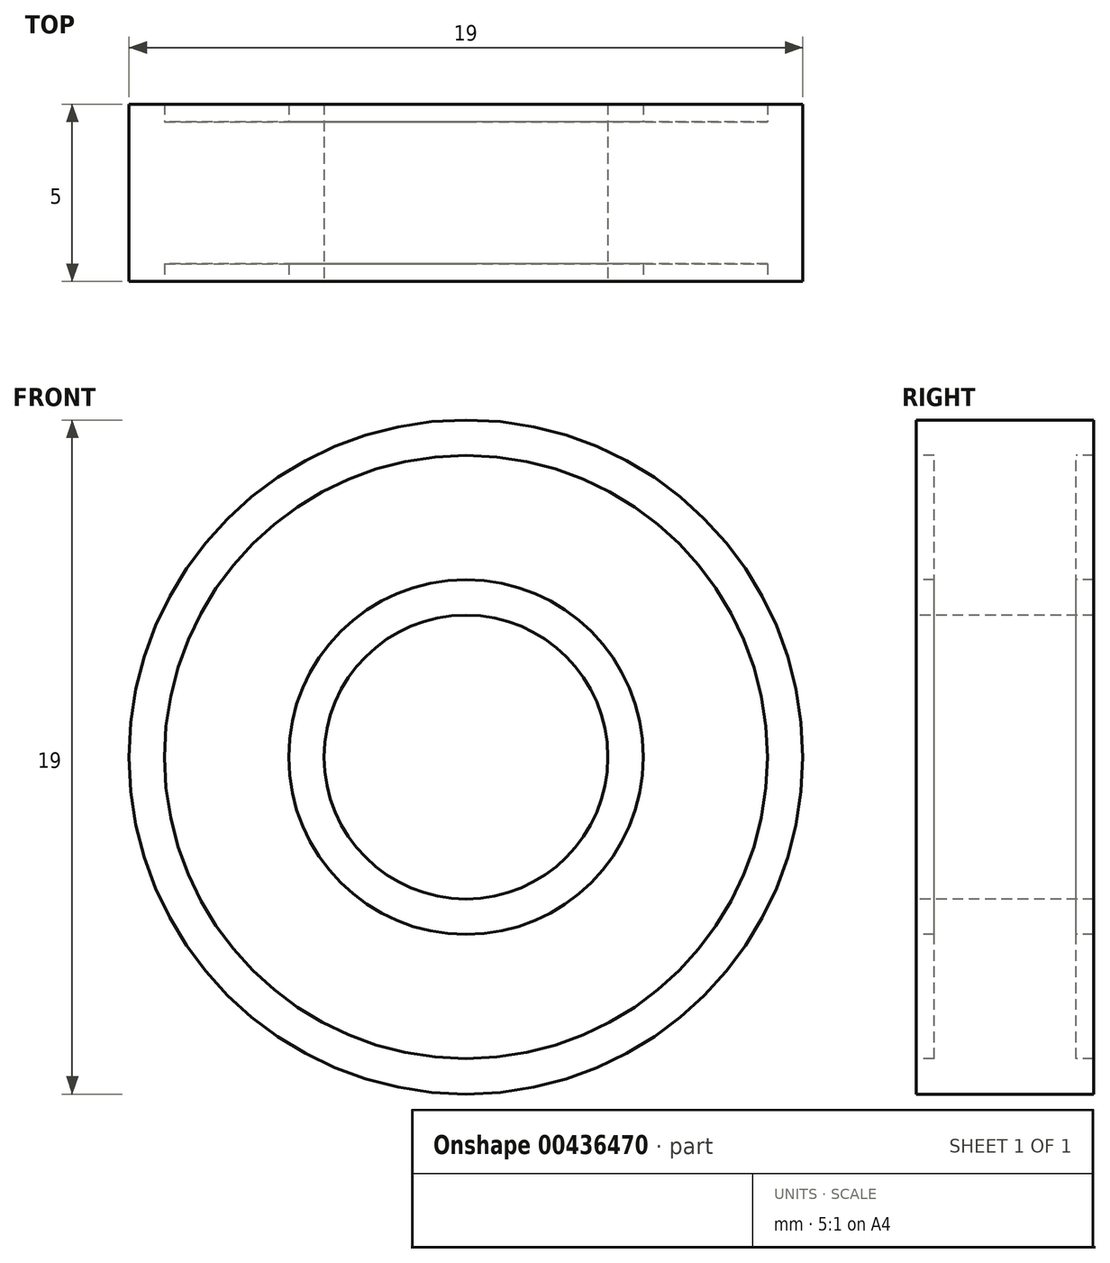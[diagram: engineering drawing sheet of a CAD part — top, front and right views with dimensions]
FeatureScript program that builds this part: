
annotation { "Feature Type Name" : "Feature", "Feature Type Description" : "" }
export const myFeature = defineFeature(function(context is Context, id is Id, definition is map)
    precondition{}
    {
        {
            var Q0;
            Q0=qCreatedBy(makeId("Right.planeOp"),FACE);
            var sketch = newSketch(context, id + "F0", { "sketchPlane" : qUnion([Q0])});
            skLineSegment(sketch, "E0", {"start": v(-2.5, 4) * mm, "end": v(2.5, 4) * mm});
            skLineSegment(sketch, "E1", {"start": v(2.5, 4) * mm, "end": v(2.5, 5) * mm});
            skLineSegment(sketch, "E2", {"start": v(2.5, 5) * mm, "end": v(2, 5) * mm});
            skLineSegment(sketch, "E3", {"start": v(2, 5) * mm, "end": v(2, 8.5) * mm});
            skLineSegment(sketch, "E4", {"start": v(2, 8.5) * mm, "end": v(2.5, 8.5) * mm});
            skLineSegment(sketch, "E5", {"start": v(2.5, 8.5) * mm, "end": v(2.5, 9.5) * mm});
            skLineSegment(sketch, "E6", {"start": v(2.5, 9.5) * mm, "end": v(-2.5, 9.5) * mm});
            skLineSegment(sketch, "E7", {"start": v(-2.5, 9.5) * mm, "end": v(-2.5, 8.5) * mm});
            skLineSegment(sketch, "E8", {"start": v(-2.5, 8.5) * mm, "end": v(-2, 8.5) * mm});
            skLineSegment(sketch, "E9", {"start": v(-2, 8.5) * mm, "end": v(-2, 5) * mm});
            skLineSegment(sketch, "E10", {"start": v(-2, 5) * mm, "end": v(-2.5, 5) * mm});
            skLineSegment(sketch, "E11", {"start": v(-2.5, 5) * mm, "end": v(-2.5, 4) * mm});
            skLineSegment(sketch, "E12", {"start": v(-12.07, 0) * mm, "end": v(10.29, 0) * mm});
            skSolve(sketch);
        }
        {
            var Q0;
            Q0=makeQuery(id+"F0.imprint","IMPRINT",FACE,{"disambiguationData":[TD([[makeQuery(id+"F0.imprint","IMPRINT",EDGE,{"derivedFrom":sQuery(id+"F0.wireOp",EDGE,"E0")}),1.0]])]});
            var Q1;
            Q1=sQuery(id+"F0.wireOp",EDGE,"E12");
            revolve(context, id + "F1", {"entities" : qUnion([Q0]), "axis" : qUnion([Q1]), "revolveType" : RevolveType.FULL});
        }
    });
